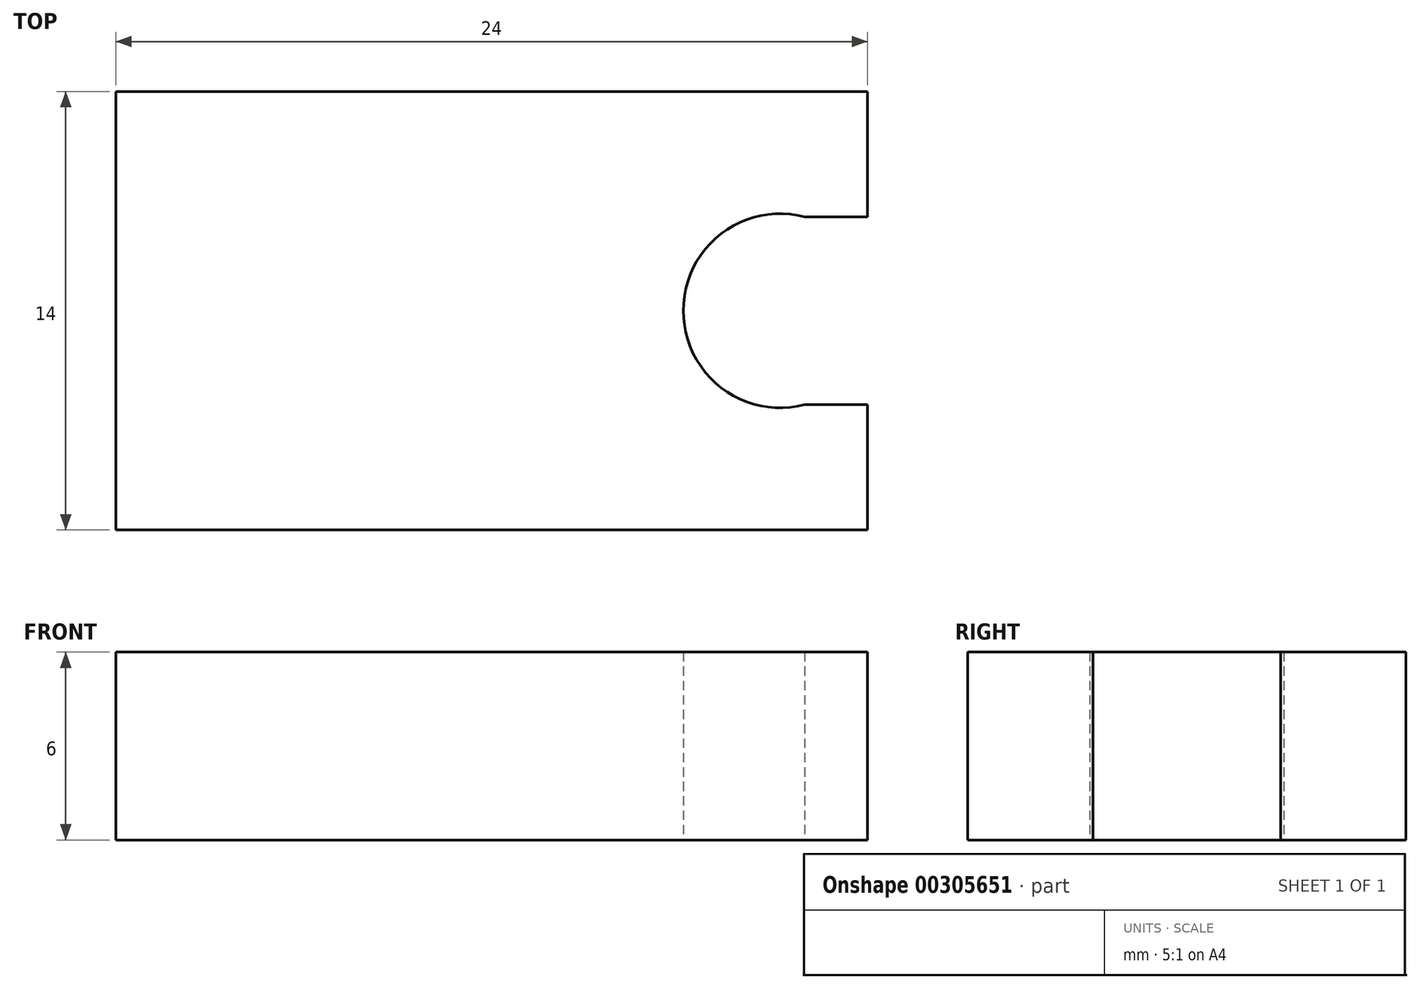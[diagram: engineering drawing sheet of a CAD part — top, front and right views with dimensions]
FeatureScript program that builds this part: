
annotation { "Feature Type Name" : "Feature", "Feature Type Description" : "" }
export const myFeature = defineFeature(function(context is Context, id is Id, definition is map)
    precondition{}
    {
        {
            var Q0;
            Q0=qCreatedBy(makeId("Top.planeOp"),FACE);
            var sketch = newSketch(context, id + "F0", { "sketchPlane" : qUnion([Q0])});
            skLineSegment(sketch, "E0.bottom", {"start": v(12, -7) * mm, "end": v(-12, -7) * mm});
            skLineSegment(sketch, "E0.top", {"start": v(12, 7) * mm, "end": v(-12, 7) * mm});
            skLineSegment(sketch, "E0.right", {"start": v(-12, -7) * mm, "end": v(-12, 7) * mm});
            skPoint(sketch, "E0.middle", {"position": v(0, 0) * mm});
            skLineSegment(sketch, "E1", {"start": v(12, 7) * mm, "end": v(12, 3) * mm});
            skLineSegment(sketch, "E2", {"start": v(12, -7) * mm, "end": v(12, -3) * mm});
            skLineSegment(sketch, "E3", {"start": v(12, 3) * mm, "end": v(10, 3) * mm});
            skLineSegment(sketch, "E4", {"start": v(12, -3) * mm, "end": v(10, -3) * mm});
            skArc(sketch, "E5", {"start": v(10, 3) * mm, "mid": v(6.12, 0) * mm, "end": v(10, -3) * mm});
            skSolve(sketch);
        }
        {
            var Q0;
            Q0 = qSketchRegion(id + "F0", true);
            extrude(context, id + "F1", {"entities" : qUnion([Q0]), "depth" : 6 * mm});
        }
    });
